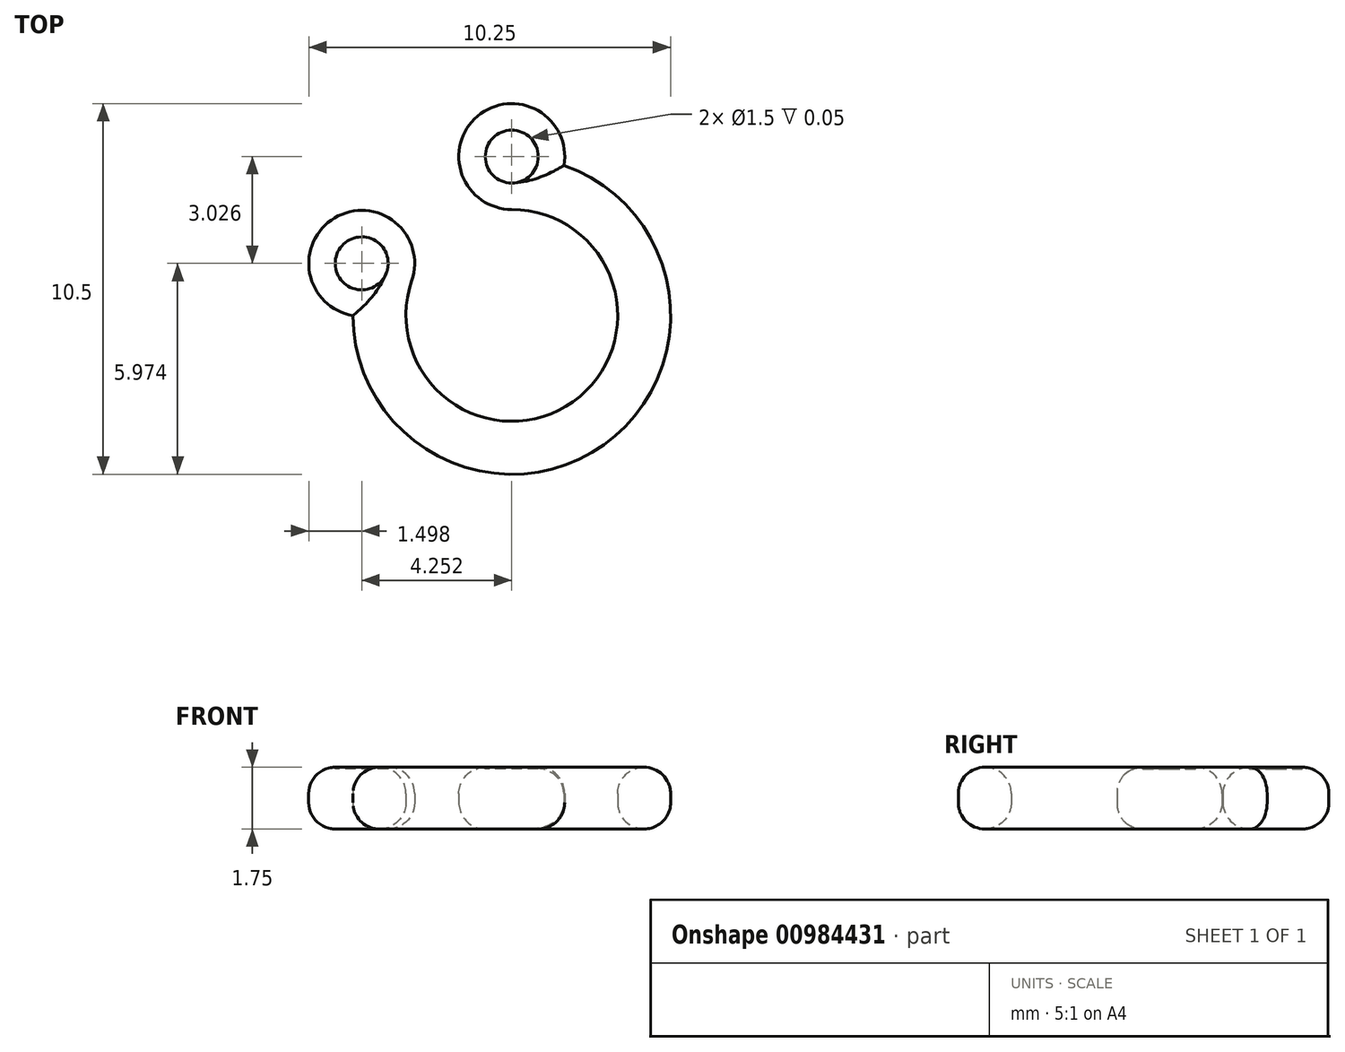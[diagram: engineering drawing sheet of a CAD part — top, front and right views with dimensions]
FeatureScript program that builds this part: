
annotation { "Feature Type Name" : "Feature", "Feature Type Description" : "" }
export const myFeature = defineFeature(function(context is Context, id is Id, definition is map)
    precondition{}
    {
        {
            var Q0;
            Q0=qCreatedBy(makeId("Top.planeOp"),FACE);
            var sketch = newSketch(context, id + "F0", { "sketchPlane" : qUnion([Q0])});
            skLineSegment(sketch, "E0", {"start": v(0, 0) * mm, "end": v(-4.72, 1.64) * mm, "construction": true});
            skCircle(sketch, "E1", {"center": v(0, 0) * mm, "radius": 3 * mm, "construction": true});
            skArc(sketch, "E2", {"start": v(0, 3) * mm, "mid": v(1.74, -2.44) * mm, "end": v(-2.83, 0.98) * mm});
            skLineSegment(sketch, "E3", {"start": v(0, 0) * mm, "end": v(0, 4.5) * mm, "construction": true});
            skArc(sketch, "E4", {"start": v(0, 4.5) * mm, "mid": v(2.6, -3.67) * mm, "end": v(-4.25, 1.47) * mm});
            skArc(sketch, "E5", {"start": v(-2.83, 0.98) * mm, "mid": v(-5.02, 2.76) * mm, "end": v(-4.5, 0) * mm});
            skArc(sketch, "E6", {"start": v(0, 3) * mm, "mid": v(-0.97, 5.65) * mm, "end": v(1.48, 4.25) * mm});
            skSolve(sketch);
        }
        {
            var Q0;
            Q0 = qSketchRegion(id + "F0", true);
            extrude(context, id + "F1", {"entities" : qUnion([Q0]), "depth" : 1.75 * mm, "offsetDistance" : 25 * mm});
        }
        {
            var Q0;
            Q0=makeQuery(id+"F1.opExtrude","CAP_EDGE",EDGE,{"disambiguationData":[OSD([sQuery(id+"F0.wireOp",EDGE,"E4")])],"isStart":false});
            var Q1;
            Q1=makeQuery(id+"F1.opExtrude","CAP_EDGE",EDGE,{"disambiguationData":[OSD([sQuery(id+"F0.wireOp",EDGE,"E4")])],"isStart":true});
            var Q2;
            Q2=makeQuery(id+"F1.opExtrude","CAP_EDGE",EDGE,{"disambiguationData":[OSD([sQuery(id+"F0.wireOp",EDGE,"E2")])],"isStart":false});
            var Q3;
            Q3=makeQuery(id+"F1.opExtrude","CAP_EDGE",EDGE,{"disambiguationData":[OSD([sQuery(id+"F0.wireOp",EDGE,"E2")])],"isStart":true});
            fillet(context, id + "F2", {"entities" : qUnion([Q0, Q1, Q2, Q3]), "radius" : 0.75 * mm, "tangentPropagation" : true, "allowEdgeOverflow" : false});
        }
        {
            var Q0;
            Q0=makeQuery(id+"F2.opFillet","SPLIT",FACE,{"disambiguationData":[OD(0.0)],"derivedFrom":makeQuery(id+"F1.opExtrude","CAP_FACE",FACE,{"disambiguationData":[OSD([sQuery(id+"F0.wireOp",EDGE,"E2"),sQuery(id+"F0.wireOp",EDGE,"E4"),sQuery(id+"F0.wireOp",EDGE,"E5"),sQuery(id+"F0.wireOp",EDGE,"E6")])],"isStart":false})});
            var Q1;
            Q1=makeQuery(id+"F2.opFillet","SPLIT",FACE,{"disambiguationData":[OD(1.0)],"derivedFrom":makeQuery(id+"F1.opExtrude","CAP_FACE",FACE,{"disambiguationData":[OSD([sQuery(id+"F0.wireOp",EDGE,"E2"),sQuery(id+"F0.wireOp",EDGE,"E4"),sQuery(id+"F0.wireOp",EDGE,"E5"),sQuery(id+"F0.wireOp",EDGE,"E6")])],"isStart":false})});
            extrude(context, id + "F3", {"entities" : qUnion([Q0, Q1]), "operationType" : NewBodyOperationType.REMOVE, "oppositeDirection" : true, "depth" : 0.05 * mm, "offsetDistance" : 25 * mm});
        }
    });
